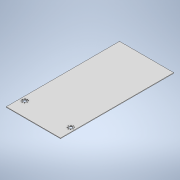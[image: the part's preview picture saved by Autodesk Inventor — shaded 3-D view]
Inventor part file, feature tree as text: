
AUTODESK INVENTOR PART (.ipt)
format: ipt  version: 2020 (Build 240168000, 168)  size: 174,592 bytes
history: native  units: in
note: dims shown in document units (in); Inventor stores cm internally (conversion verified against a paired STEP export)
features: extrude x3, sketch x3
ambient origin geometry x8: Origin, YZ Plane, XZ Plane, XY Plane, X Axis, Y Axis, Z Axis, Center Point
bodies: Solid1 (feature_tree)
feature tree (6):
  extrude  "Extrusion1"  Depth=8.5in
  extrude  "Extrusion2"  Depth=0.09in
  extrude  "Extrusion3"  Depth=0.09in
  sketch  "Sketch1"  dims[d0=8.5in d1=17.5in]
  sketch  "Sketch2"  dims[d2=0.09in d3=0.0in d5=0.5in]
  sketch  "Sketch3"  dims[d6=0.5in d23=0.1406in d24=0.1406in d25=0.1406in d26=0.1406in d27=0.1406in d28=0.1406in d29=0.1406in d30=0.1406in d31=0.5in d32=0.1406in d33=0.1406in d34=0.1406in d35=0.1406in d36=0.1406in d37=0.1406in d38=0.1406in d39=0.1406in d49=0.5in d50=0.1406in d51=0.1406in d52=0.1406in d53=0.1406in d54=0.1406in d56=0.1406in d57=0.1406in d62=0.1406in d63=0.1406in d64=0.1406in d85=0.09in d86=0.0in d148=0.2504in d149=0.0in]
